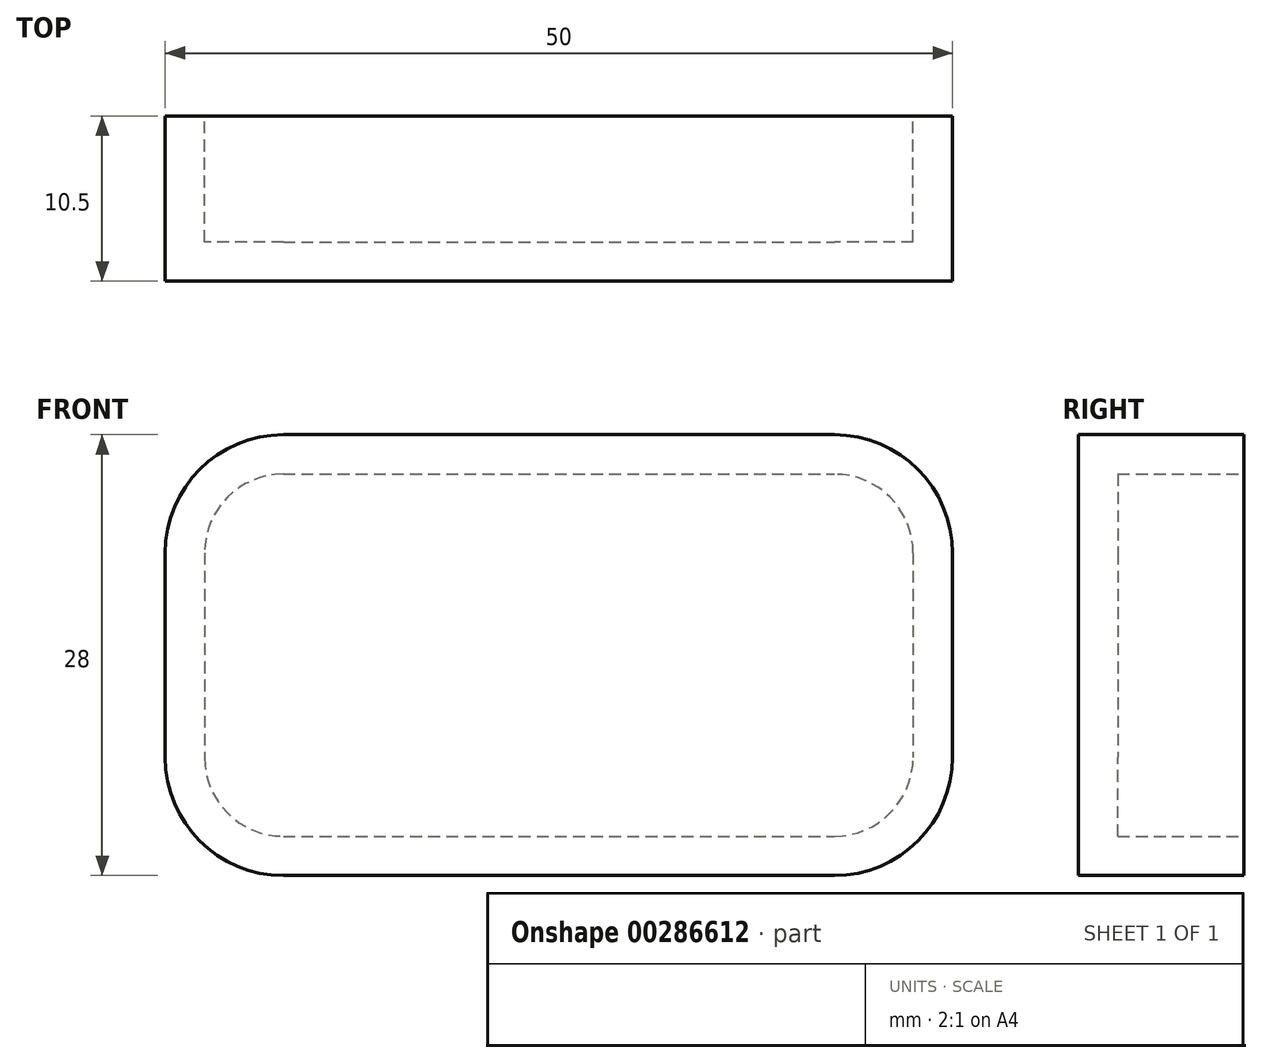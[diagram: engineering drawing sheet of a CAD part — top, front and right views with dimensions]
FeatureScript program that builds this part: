
annotation { "Feature Type Name" : "Feature", "Feature Type Description" : "" }
export const myFeature = defineFeature(function(context is Context, id is Id, definition is map)
    precondition{}
    {
        {
            var Q0;
            Q0=qCreatedBy(makeId("Front.planeOp"),FACE);
            var sketch = newSketch(context, id + "F0", { "sketchPlane" : qUnion([Q0])});
            skLineSegment(sketch, "E0.bottom", {"start": v(-22.5, 11.5) * mm, "end": v(22.5, 11.5) * mm});
            skLineSegment(sketch, "E0.top", {"start": v(-22.5, -11.5) * mm, "end": v(22.5, -11.5) * mm});
            skLineSegment(sketch, "E0.left", {"start": v(-22.5, 11.5) * mm, "end": v(-22.5, -11.5) * mm});
            skLineSegment(sketch, "E0.right", {"start": v(22.5, 11.5) * mm, "end": v(22.5, -11.5) * mm});
            skPoint(sketch, "E0.middle", {"position": v(0, 0) * mm});
            skSolve(sketch);
        }
        {
            var Q0;
            Q0=makeQuery(id+"F0.imprint","IMPRINT",FACE,{"disambiguationData":[TD([[makeQuery(id+"F0.imprint","IMPRINT",EDGE,{"derivedFrom":sQuery(id+"F0.wireOp",EDGE,"E0.bottom")}),-1.0]])]});
            extrude(context, id + "F1", {"entities" : qUnion([Q0]), "depth" : 8 * mm});
        }
        {
            var Q0;
            Q0=makeQuery(id+"F1.opExtrude","SWEPT_EDGE",EDGE,{"disambiguationData":[OSD([sQuery(id+"F0.wireOp",EDGE,"E0.bottom"),sQuery(id+"F0.wireOp",EDGE,"E0.right")])]});
            var Q1;
            Q1=makeQuery(id+"F1.opExtrude","SWEPT_EDGE",EDGE,{"disambiguationData":[OSD([sQuery(id+"F0.wireOp",EDGE,"E0.bottom"),sQuery(id+"F0.wireOp",EDGE,"E0.left")])]});
            var Q2;
            Q2=makeQuery(id+"F1.opExtrude","SWEPT_EDGE",EDGE,{"disambiguationData":[OSD([sQuery(id+"F0.wireOp",EDGE,"E0.top"),sQuery(id+"F0.wireOp",EDGE,"E0.right")])]});
            var Q3;
            Q3=makeQuery(id+"F1.opExtrude","SWEPT_EDGE",EDGE,{"disambiguationData":[OSD([sQuery(id+"F0.wireOp",EDGE,"E0.top"),sQuery(id+"F0.wireOp",EDGE,"E0.left")])]});
            fillet(context, id + "F2", {"entities" : qUnion([Q0, Q1, Q2, Q3]), "radius" : 5 * mm, "tangentPropagation" : true, "allowEdgeOverflow" : false});
        }
        {
            var Q0;
            Q0=makeQuery(id+"F1.opExtrude","CAP_FACE",FACE,{"disambiguationData":[OSD([sQuery(id+"F0.wireOp",EDGE,"E0.bottom"),sQuery(id+"F0.wireOp",EDGE,"E0.top"),sQuery(id+"F0.wireOp",EDGE,"E0.left"),sQuery(id+"F0.wireOp",EDGE,"E0.right")])],"isStart":true});
            shell(context, id + "F3", {"entities" : qUnion([Q0]), "thickness" : 2.5 * mm, "oppositeDirection" : true});
        }
    });
